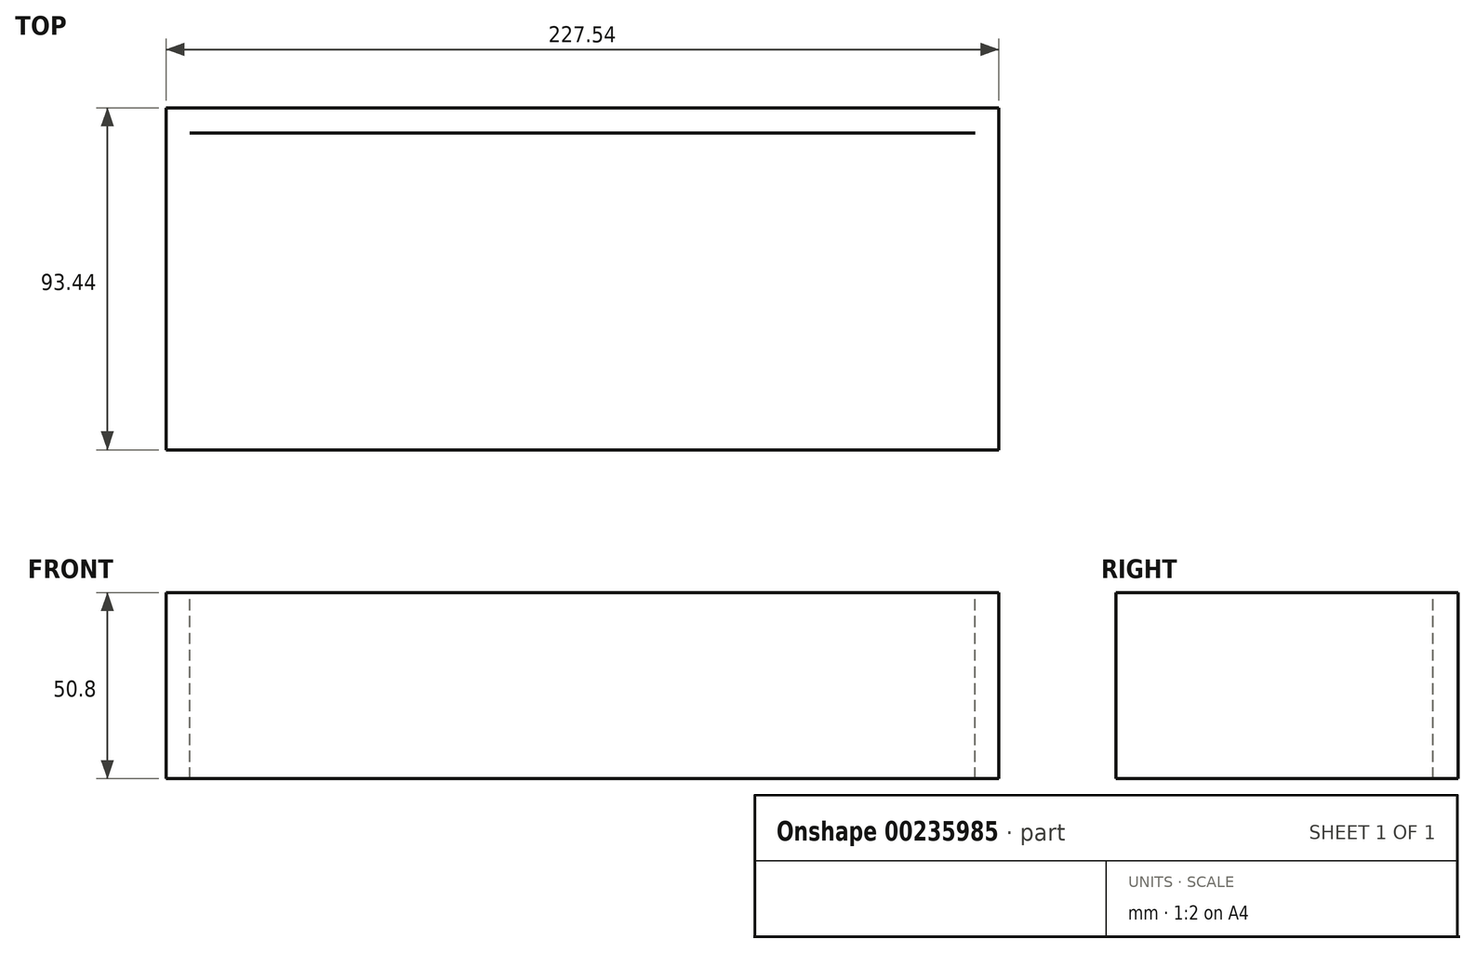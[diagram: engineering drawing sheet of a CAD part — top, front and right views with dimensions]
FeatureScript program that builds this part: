
annotation { "Feature Type Name" : "Feature", "Feature Type Description" : "" }
export const myFeature = defineFeature(function(context is Context, id is Id, definition is map)
    precondition{}
    {
        {
            var Q0;
            Q0=qCreatedBy(makeId("Top.planeOp"),FACE);
            var sketch = newSketch(context, id + "F0", { "sketchPlane" : qUnion([Q0])});
            skLineSegment(sketch, "E0.bottom", {"start": v(-107.29, 39.94) * mm, "end": v(107.29, 39.94) * mm});
            skLineSegment(sketch, "E0.top", {"start": v(-107.29, -39.94) * mm, "end": v(107.29, -39.94) * mm});
            skLineSegment(sketch, "E0.left", {"start": v(-107.29, 39.94) * mm, "end": v(-107.29, -39.94) * mm});
            skLineSegment(sketch, "E0.right", {"start": v(107.29, 39.94) * mm, "end": v(107.29, -39.94) * mm});
            skPoint(sketch, "E0.middle", {"position": v(0, 0) * mm});
            skLineSegment(sketch, "E1.bottom", {"start": v(-113.77, 46.72) * mm, "end": v(113.77, 46.72) * mm});
            skLineSegment(sketch, "E1.top", {"start": v(-113.77, -46.72) * mm, "end": v(113.77, -46.72) * mm});
            skLineSegment(sketch, "E1.left", {"start": v(-113.77, 46.72) * mm, "end": v(-113.77, -46.72) * mm});
            skLineSegment(sketch, "E1.right", {"start": v(113.77, 46.72) * mm, "end": v(113.77, -46.72) * mm});
            skSolve(sketch);
        }
        {
            var Q0;
            Q0=sQuery(id+"F0.wireOp",EDGE,"E1.bottom");
            var Q1;
            Q1=sQuery(id+"F0.wireOp",EDGE,"E1.left");
            var Q2;
            Q2=sQuery(id+"F0.wireOp",EDGE,"E1.top");
            var Q3;
            Q3=sQuery(id+"F0.wireOp",EDGE,"E1.right");
            var Q4;
            Q4=sQuery(id+"F0.wireOp",EDGE,"E0.bottom");
            extrude(context, id + "F1", {"bodyType" : ToolBodyType.SURFACE, "surfaceEntities" : qUnion([Q0, Q1, Q2, Q3, Q4]), "depth" : 50.8 * mm});
        }
    });
